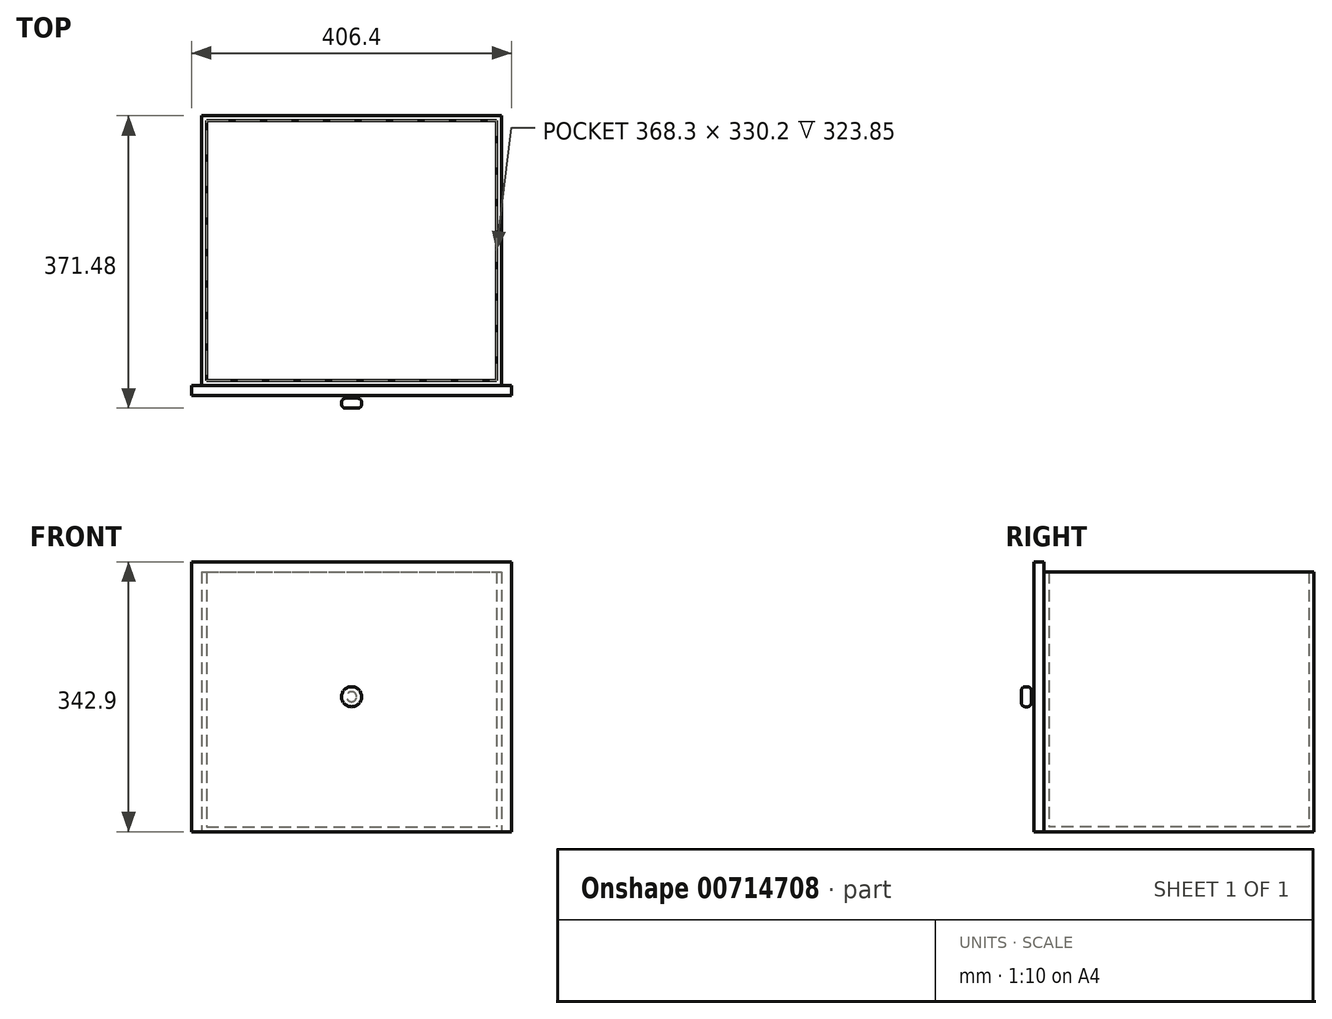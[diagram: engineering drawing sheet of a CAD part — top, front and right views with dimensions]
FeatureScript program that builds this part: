
annotation { "Feature Type Name" : "Feature", "Feature Type Description" : "" }
export const myFeature = defineFeature(function(context is Context, id is Id, definition is map)
    precondition{}
    {
        {
            var Q0;
            Q0=qCreatedBy(makeId("Top.planeOp"),FACE);
            var sketch = newSketch(context, id + "F0", { "sketchPlane" : qUnion([Q0])});
            skLineSegment(sketch, "E0.bottom", {"start": v(-107.13, 192.89) * mm, "end": v(273.87, 192.89) * mm});
            skLineSegment(sketch, "E0.top", {"start": v(-107.13, -150.01) * mm, "end": v(273.87, -150.01) * mm});
            skLineSegment(sketch, "E0.left", {"start": v(-107.13, 192.89) * mm, "end": v(-107.13, -150.01) * mm});
            skLineSegment(sketch, "E0.right", {"start": v(273.87, 192.89) * mm, "end": v(273.87, -150.01) * mm});
            skSolve(sketch);
        }
        {
            var Q0;
            Q0 = qSketchRegion(id + "F0", true);
            extrude(context, id + "F1", {"entities" : qUnion([Q0]), "depth" : 330.2 * mm, "offsetDistance" : 25.4 * mm});
        }
        {
            var Q0;
            Q0=makeQuery(id+"F1.opExtrude","CAP_FACE",FACE,{"disambiguationData":[OSD([sQuery(id+"F0.wireOp",EDGE,"E0.bottom"),sQuery(id+"F0.wireOp",EDGE,"E0.top"),sQuery(id+"F0.wireOp",EDGE,"E0.left"),sQuery(id+"F0.wireOp",EDGE,"E0.right")])],"isStart":false});
            shell(context, id + "F2", {"entities" : qUnion([Q0]), "thickness" : 6.35 * mm});
        }
        {
            var Q0;
            Q0=makeQuery(id+"F1.opExtrude","SWEPT_FACE",FACE,{"disambiguationData":[OSD([sQuery(id+"F0.wireOp",EDGE,"E0.top")])]});
            var sketch = newSketch(context, id + "F3", { "sketchPlane" : qUnion([Q0])});
            skLineSegment(sketch, "E1.top", {"start": v(286.57, 342.9) * mm, "end": v(-119.83, 342.9) * mm});
            skLineSegment(sketch, "E1.left", {"start": v(286.57, 0) * mm, "end": v(286.57, 342.9) * mm});
            skLineSegment(sketch, "E1.right", {"start": v(-119.83, 0) * mm, "end": v(-119.83, 342.9) * mm});
            skPoint(sketch, "E1.middle", {"position": v(83.37, 165.1) * mm});
            skPoint(sketch, "E2.orphan", {"position": v(-107.13, 330.2) * mm});
            skPoint(sketch, "E3.end.orphan", {"position": v(273.87, 0) * mm});
            skLineSegment(sketch, "E4", {"start": v(-107.13, 0) * mm, "end": v(-119.83, 0) * mm});
            skLineSegment(sketch, "E5", {"start": v(273.87, 0) * mm, "end": v(286.57, 0) * mm});
            skPoint(sketch, "E1.bottom.end.orphan", {"position": v(-119.83, -12.7) * mm});
            skPoint(sketch, "E6.orphan", {"position": v(286.57, -12.7) * mm});
            skLineSegment(sketch, "E7", {"start": v(-107.13, 0) * mm, "end": v(273.87, 0) * mm});
            skSolve(sketch);
        }
        {
            var Q0;
            Q0 = qSketchRegion(id + "F3", true);
            extrude(context, id + "F4", {"entities" : qUnion([Q0]), "operationType" : NewBodyOperationType.ADD, "depth" : 12.7 * mm, "offsetDistance" : 25.4 * mm});
        }
        {
            var Q0;
            Q0=makeQuery(id+"F4.opExtrude","CAP_FACE",FACE,{"disambiguationData":[OSD([sQuery(id+"F3.wireOp",EDGE,"E1.top"),sQuery(id+"F3.wireOp",EDGE,"E1.left"),sQuery(id+"F3.wireOp",EDGE,"E1.right"),sQuery(id+"F3.wireOp",EDGE,"E4"),sQuery(id+"F3.wireOp",EDGE,"E5"),sQuery(id+"F3.wireOp",EDGE,"E7")])],"isStart":false});
            var sketch = newSketch(context, id + "F5", { "sketchPlane" : qUnion([Q0])});
            skCircle(sketch, "E8", {"center": v(83.37, 171.45) * mm, "radius": 6.35 * mm});
            skPoint(sketch, "E9.trimOffspring.end.orphan", {"position": v(-119.83, 0) * mm});
            skPoint(sketch, "E10.start.orphan", {"position": v(286.57, 342.9) * mm});
            skSolve(sketch);
        }
        {
            var Q0;
            Q0 = qSketchRegion(id + "F5", true);
            extrude(context, id + "F6", {"entities" : qUnion([Q0]), "operationType" : NewBodyOperationType.ADD, "depth" : 3.17 * mm, "offsetDistance" : 25.4 * mm});
        }
        {
            var Q0;
            Q0=makeQuery(id+"F6.opExtrude","CAP_FACE",FACE,{"disambiguationData":[OSD([sQuery(id+"F5.wireOp",EDGE,"E8")])],"isStart":false});
            var sketch = newSketch(context, id + "F7", { "sketchPlane" : qUnion([Q0])});
            skCircle(sketch, "E11", {"center": v(83.37, 171.45) * mm, "radius": 12.7 * mm});
            skSolve(sketch);
        }
        {
            var Q0;
            Q0 = qSketchRegion(id + "F7", true);
            extrude(context, id + "F8", {"entities" : qUnion([Q0]), "operationType" : NewBodyOperationType.ADD, "depth" : 12.7 * mm, "offsetDistance" : 25.4 * mm});
        }
        {
            var Q0;
            Q0=makeQuery(id+"F8.opExtrude","CAP_FACE",FACE,{"disambiguationData":[OSD([sQuery(id+"F7.wireOp",EDGE,"E11")])],"isStart":false});
            var Q1;
            Q1=makeQuery(id+"F8.opExtrude","CAP_EDGE",EDGE,{"disambiguationData":[OSD([sQuery(id+"F7.wireOp",EDGE,"E11")])],"isStart":true});
            fillet(context, id + "F9", {"entities" : qUnion([Q0, Q1]), "radius" : 5.08 * mm, "tangentPropagation" : true, "allowEdgeOverflow" : false});
        }
    });
